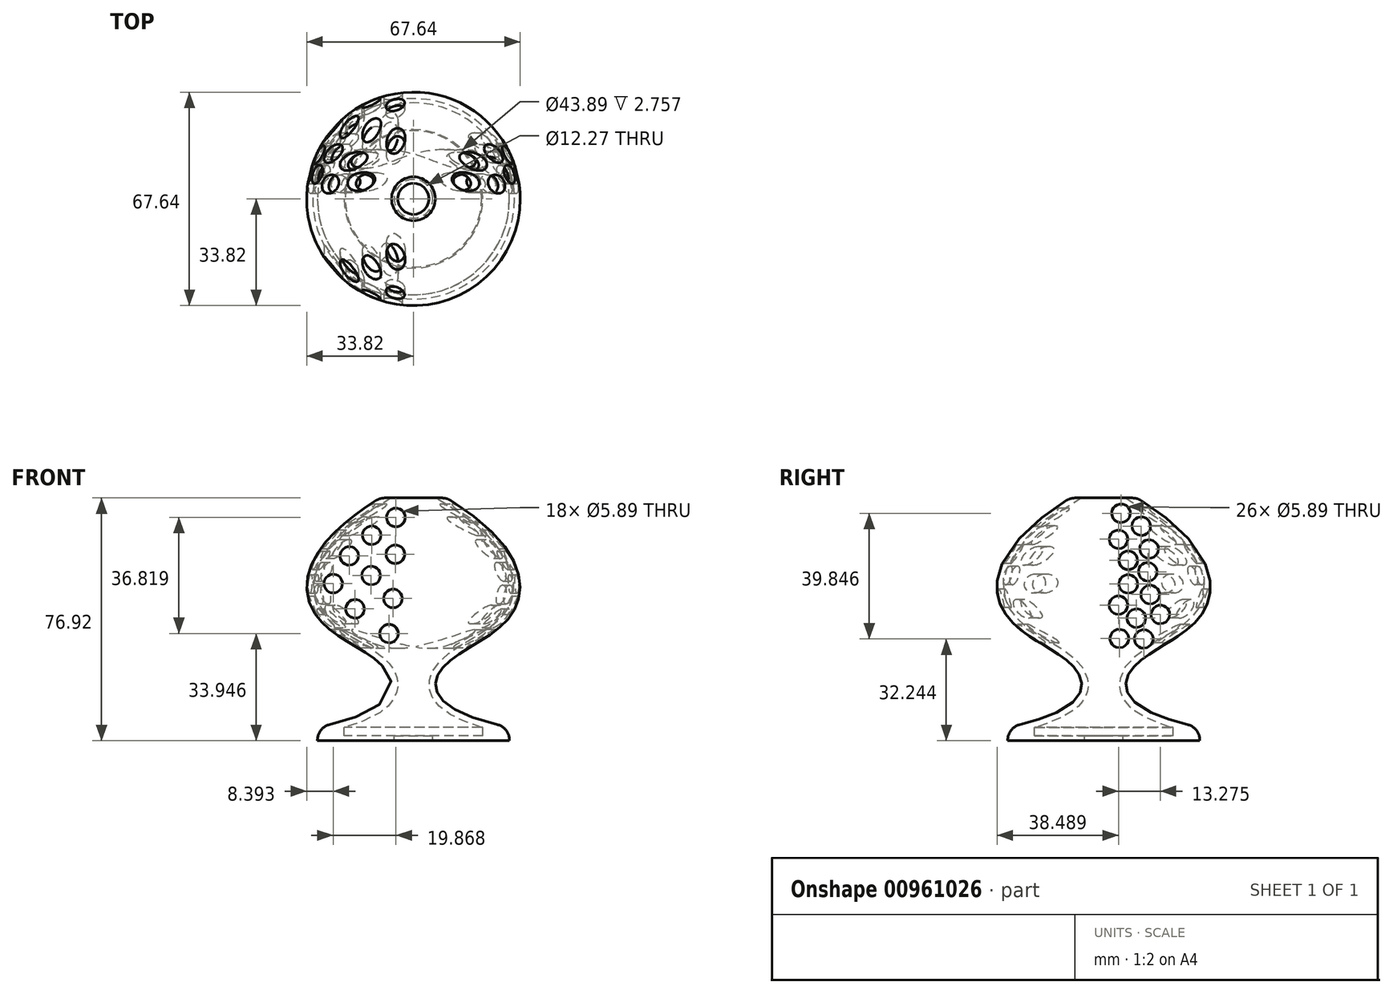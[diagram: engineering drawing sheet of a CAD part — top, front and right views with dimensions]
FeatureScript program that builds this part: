
annotation { "Feature Type Name" : "Feature", "Feature Type Description" : "" }
export const myFeature = defineFeature(function(context is Context, id is Id, definition is map)
    precondition{}
    {
        {
            var Q0;
            Q0=qCreatedBy(makeId("Front.planeOp"),FACE);
            var sketch = newSketch(context, id + "F0", { "sketchPlane" : qUnion([Q0])});
            skLineSegment(sketch, "E0", {"start": v(0, 0) * mm, "end": v(-30.41, 0) * mm});
            skFitSpline(sketch, "E1", {"points": [v(-30.41, 0) * mm, v(-9.34, 18.95) * mm, v(-30.19, 34.63) * mm, v(0, 78.45) * mm], "startDerivative": vector(248.38, 50.2) * mm, "endDerivative": vector(258.38, 128.89) * mm});
            skLineSegment(sketch, "E2", {"start": v(0, 78.45) * mm, "end": v(0, 74.71) * mm});
            skFitSpline(sketch, "E3.0", {"points": [v(-30.02, -1.96) * mm, v(-27.39, -1.43) * mm, v(-22.63, -0.3) * mm, v(-16.88, 1.6) * mm, v(-12.37, 3.66) * mm, v(-8.97, 5.91) * mm, v(-6.97, 7.97) * mm, v(-5.87, 9.74) * mm, v(-5.3, 11.12) * mm, v(-5, 12.53) * mm, v(-4.95, 13.93) * mm, v(-5.14, 15.3) * mm, v(-5.66, 17.02) * mm, v(-6.74, 19) * mm, v(-8.5, 21.08) * mm, v(-10.59, 22.92) * mm, v(-13.68, 25.15) * mm, v(-17.92, 27.7) * mm, v(-22.16, 30.28) * mm, v(-25.2, 32.5) * mm, v(-26.9, 33.99) * mm, v(-28.1, 35.24) * mm, v(-29.18, 36.54) * mm, v(-30.31, 38.27) * mm, v(-31.27, 40.51) * mm, v(-31.8, 42.9) * mm, v(-31.87, 45.48) * mm, v(-31.4, 48.25) * mm, v(-30.33, 51.24) * mm, v(-27.96, 55.49) * mm, v(-23.07, 61.28) * mm, v(-13.54, 68.77) * mm, v(-4.43, 74.01) * mm, v(0.9, 76.66) * mm]});
            skLineSegment(sketch, "E4", {"start": v(0, 70.9) * mm, "end": v(0, -14.77) * mm, "construction": true});
            skCircle(sketch, "E5", {"center": v(-5.56, 66.52) * mm, "radius": 2.94 * mm});
            skCircle(sketch, "E6", {"center": v(-13.21, 60.87) * mm, "radius": 2.94 * mm});
            skCircle(sketch, "E7", {"center": v(-5.74, 54.86) * mm, "radius": 2.94 * mm});
            skCircle(sketch, "E8", {"center": v(-13.4, 48.12) * mm, "radius": 2.94 * mm});
            skCircle(sketch, "E9", {"center": v(-6.47, 40.82) * mm, "radius": 2.94 * mm});
            skCircle(sketch, "E10", {"center": v(-7.75, 29.7) * mm, "radius": 2.94 * mm});
            skCircle(sketch, "E11", {"center": v(-18.5, 37.54) * mm, "radius": 2.94 * mm});
            skCircle(sketch, "E12", {"center": v(-25.43, 45.56) * mm, "radius": 2.94 * mm});
            skCircle(sketch, "E13", {"center": v(-20.32, 54.31) * mm, "radius": 2.94 * mm});
            skCircle(sketch, "E14.MirrorC", {"center": v(5.56, 66.52) * mm, "radius": 2.94 * mm});
            skCircle(sketch, "E15.MirrorC", {"center": v(25.43, 45.56) * mm, "radius": 2.94 * mm});
            skCircle(sketch, "E16.MirrorC", {"center": v(13.4, 48.12) * mm, "radius": 2.94 * mm});
            skCircle(sketch, "E17.MirrorC", {"center": v(7.75, 29.7) * mm, "radius": 2.94 * mm});
            skCircle(sketch, "E18.MirrorC", {"center": v(13.21, 60.87) * mm, "radius": 2.94 * mm});
            skCircle(sketch, "E19.MirrorC", {"center": v(6.47, 40.82) * mm, "radius": 2.94 * mm});
            skCircle(sketch, "E20.MirrorC", {"center": v(18.5, 37.54) * mm, "radius": 2.94 * mm});
            skCircle(sketch, "E21.MirrorC", {"center": v(5.74, 54.86) * mm, "radius": 2.94 * mm});
            skCircle(sketch, "E22.MirrorC", {"center": v(20.32, 54.31) * mm, "radius": 2.94 * mm});
            skLineSegment(sketch, "E23", {"start": v(-30.41, 0) * mm, "end": v(-30.41, -4.24) * mm});
            skLineSegment(sketch, "E24", {"start": v(-30.41, -4.24) * mm, "end": v(0, -4.24) * mm});
            skLineSegment(sketch, "E25", {"start": v(-21.94, 0) * mm, "end": v(-21.94, -2.76) * mm});
            skLineSegment(sketch, "E26", {"start": v(-21.94, -2.76) * mm, "end": v(0, -2.76) * mm});
            skLineSegment(sketch, "E27", {"start": v(0, -2.76) * mm, "end": v(0, -4.24) * mm});
            skSolve(sketch);
        }
        {
            var Q0;
            {var subQ0=sQuery(id+"F0.wireOp",EDGE,"E1");Q0=makeQuery(id+"F0.imprint","IMPRINT",FACE,{"disambiguationData":[TD([[makeQuery(id+"F0.imprint","IMPRINT",EDGE,{"derivedFrom":subQ0}),-1.0]])]});}
            var Q1;
            {var subQ1=sQuery(id+"F0.wireOp",EDGE,"E23");Q1=makeQuery(id+"F0.imprint","IMPRINT",FACE,{"disambiguationData":[TD([[makeQuery(id+"F0.imprint","IMPRINT",EDGE,{"derivedFrom":subQ1}),1.0]])]});}
            var Q2;
            Q2=sQuery(id+"F0.wireOp",EDGE,"E4");
            revolve(context, id + "F1", {"surfaceOperationType" : NewSurfaceOperationType.NEW, "entities" : qUnion([Q0, Q1]), "axis" : qUnion([Q2]), "revolveType" : RevolveType.FULL});
        }
        {
            var Q0;
            Q0=makeQuery(id+"F0.imprint","IMPRINT",FACE,{"disambiguationData":[TD([[makeQuery(id+"F0.imprint","IMPRINT",EDGE,{"derivedFrom":sQuery(id+"F0.wireOp",EDGE,"E5")}),1.0]])]});
            var Q1;
            Q1=makeQuery(id+"F0.imprint","IMPRINT",FACE,{"disambiguationData":[TD([[makeQuery(id+"F0.imprint","IMPRINT",EDGE,{"derivedFrom":sQuery(id+"F0.wireOp",EDGE,"E14.MirrorC")}),-1.0]])]});
            var Q2;
            Q2=makeQuery(id+"F0.imprint","IMPRINT",FACE,{"disambiguationData":[TD([[makeQuery(id+"F0.imprint","IMPRINT",EDGE,{"derivedFrom":sQuery(id+"F0.wireOp",EDGE,"E21.MirrorC")}),-1.0]])]});
            var Q3;
            Q3=makeQuery(id+"F0.imprint","IMPRINT",FACE,{"disambiguationData":[TD([[makeQuery(id+"F0.imprint","IMPRINT",EDGE,{"derivedFrom":sQuery(id+"F0.wireOp",EDGE,"E18.MirrorC")}),-1.0]])]});
            var Q4;
            Q4=makeQuery(id+"F0.imprint","IMPRINT",FACE,{"disambiguationData":[TD([[makeQuery(id+"F0.imprint","IMPRINT",EDGE,{"derivedFrom":sQuery(id+"F0.wireOp",EDGE,"E22.MirrorC")}),-1.0]])]});
            var Q5;
            Q5=makeQuery(id+"F0.imprint","IMPRINT",FACE,{"disambiguationData":[TD([[makeQuery(id+"F0.imprint","IMPRINT",EDGE,{"derivedFrom":sQuery(id+"F0.wireOp",EDGE,"E16.MirrorC")}),-1.0]])]});
            var Q6;
            Q6=makeQuery(id+"F0.imprint","IMPRINT",FACE,{"disambiguationData":[TD([[makeQuery(id+"F0.imprint","IMPRINT",EDGE,{"derivedFrom":sQuery(id+"F0.wireOp",EDGE,"E19.MirrorC")}),-1.0]])]});
            var Q7;
            Q7=makeQuery(id+"F0.imprint","IMPRINT",FACE,{"disambiguationData":[TD([[makeQuery(id+"F0.imprint","IMPRINT",EDGE,{"derivedFrom":sQuery(id+"F0.wireOp",EDGE,"E17.MirrorC")}),-1.0]])]});
            var Q8;
            Q8=makeQuery(id+"F0.imprint","IMPRINT",FACE,{"disambiguationData":[TD([[makeQuery(id+"F0.imprint","IMPRINT",EDGE,{"derivedFrom":sQuery(id+"F0.wireOp",EDGE,"E20.MirrorC")}),-1.0]])]});
            var Q9;
            Q9=makeQuery(id+"F0.imprint","IMPRINT",FACE,{"disambiguationData":[TD([[makeQuery(id+"F0.imprint","IMPRINT",EDGE,{"derivedFrom":sQuery(id+"F0.wireOp",EDGE,"E15.MirrorC")}),-1.0]])]});
            var Q10;
            Q10=makeQuery(id+"F0.imprint","IMPRINT",FACE,{"disambiguationData":[TD([[makeQuery(id+"F0.imprint","IMPRINT",EDGE,{"derivedFrom":sQuery(id+"F0.wireOp",EDGE,"E7")}),1.0]])]});
            var Q11;
            Q11=makeQuery(id+"F0.imprint","IMPRINT",FACE,{"disambiguationData":[TD([[makeQuery(id+"F0.imprint","IMPRINT",EDGE,{"derivedFrom":sQuery(id+"F0.wireOp",EDGE,"E6")}),1.0]])]});
            var Q12;
            Q12=makeQuery(id+"F0.imprint","IMPRINT",FACE,{"disambiguationData":[TD([[makeQuery(id+"F0.imprint","IMPRINT",EDGE,{"derivedFrom":sQuery(id+"F0.wireOp",EDGE,"E13")}),1.0]])]});
            var Q13;
            Q13=makeQuery(id+"F0.imprint","IMPRINT",FACE,{"disambiguationData":[TD([[makeQuery(id+"F0.imprint","IMPRINT",EDGE,{"derivedFrom":sQuery(id+"F0.wireOp",EDGE,"E12")}),1.0]])]});
            var Q14;
            Q14=makeQuery(id+"F0.imprint","IMPRINT",FACE,{"disambiguationData":[TD([[makeQuery(id+"F0.imprint","IMPRINT",EDGE,{"derivedFrom":sQuery(id+"F0.wireOp",EDGE,"E11")}),1.0]])]});
            var Q15;
            Q15=makeQuery(id+"F0.imprint","IMPRINT",FACE,{"disambiguationData":[TD([[makeQuery(id+"F0.imprint","IMPRINT",EDGE,{"derivedFrom":sQuery(id+"F0.wireOp",EDGE,"E8")}),1.0]])]});
            var Q16;
            Q16=makeQuery(id+"F0.imprint","IMPRINT",FACE,{"disambiguationData":[TD([[makeQuery(id+"F0.imprint","IMPRINT",EDGE,{"derivedFrom":sQuery(id+"F0.wireOp",EDGE,"E9")}),1.0]])]});
            var Q17;
            Q17=makeQuery(id+"F0.imprint","IMPRINT",FACE,{"disambiguationData":[TD([[makeQuery(id+"F0.imprint","IMPRINT",EDGE,{"derivedFrom":sQuery(id+"F0.wireOp",EDGE,"E10")}),1.0]])]});
            extrude(context, id + "F2", {"entities" : qUnion([Q0, Q1, Q2, Q3, Q4, Q5, Q6, Q7, Q8, Q9, Q10, Q11, Q12, Q13, Q14, Q15, Q16, Q17]), "operationType" : NewBodyOperationType.REMOVE, "endBound" : BoundingType.SYMMETRIC, "oppositeDirection" : true, "depth" : 250 * mm, "offsetDistance" : 25 * mm});
        }
        {
            var Q0;
            Q0=qCreatedBy(makeId("Right.planeOp"),FACE);
            var sketch = newSketch(context, id + "F3", { "sketchPlane" : qUnion([Q0])});
            skCircle(sketch, "E28", {"center": v(5.45, 67.85) * mm, "radius": 2.94 * mm});
            skCircle(sketch, "E29", {"center": v(11.9, 63.76) * mm, "radius": 2.94 * mm});
            skCircle(sketch, "E30", {"center": v(4.67, 59.6) * mm, "radius": 2.94 * mm});
            skCircle(sketch, "E31", {"center": v(14.34, 56.53) * mm, "radius": 2.94 * mm});
            skCircle(sketch, "E32", {"center": v(7.77, 52.91) * mm, "radius": 2.94 * mm});
            skCircle(sketch, "E33", {"center": v(13.95, 49.3) * mm, "radius": 2.94 * mm});
            skCircle(sketch, "E34", {"center": v(10.34, 34.59) * mm, "radius": 2.94 * mm});
            skCircle(sketch, "E35", {"center": v(14.72, 42.07) * mm, "radius": 2.94 * mm});
            skCircle(sketch, "E36", {"center": v(12.66, 28) * mm, "radius": 2.94 * mm});
            skCircle(sketch, "E37", {"center": v(17.94, 35.75) * mm, "radius": 2.94 * mm});
            skCircle(sketch, "E38", {"center": v(4.92, 28.13) * mm, "radius": 2.94 * mm});
            skCircle(sketch, "E39", {"center": v(7.76, 45.43) * mm, "radius": 2.94 * mm});
            skCircle(sketch, "E40", {"center": v(4.67, 38.71) * mm, "radius": 2.94 * mm});
            skLineSegment(sketch, "E41", {"start": v(0, -6.38) * mm, "end": v(0, 72) * mm, "construction": true});
            skCircle(sketch, "E42.MirrorC", {"center": v(-4.92, 28.13) * mm, "radius": 2.94 * mm});
            skCircle(sketch, "E43.MirrorC", {"center": v(-12.66, 28) * mm, "radius": 2.94 * mm});
            skCircle(sketch, "E44.MirrorC", {"center": v(-17.94, 35.75) * mm, "radius": 2.94 * mm});
            skCircle(sketch, "E45.MirrorC", {"center": v(-10.34, 34.59) * mm, "radius": 2.94 * mm});
            skCircle(sketch, "E46.MirrorC", {"center": v(-4.67, 38.71) * mm, "radius": 2.94 * mm});
            skCircle(sketch, "E47.MirrorC", {"center": v(-14.72, 42.07) * mm, "radius": 2.94 * mm});
            skCircle(sketch, "E48.MirrorC", {"center": v(-7.76, 45.43) * mm, "radius": 2.94 * mm});
            skCircle(sketch, "E49.MirrorC", {"center": v(-13.95, 49.3) * mm, "radius": 2.94 * mm});
            skCircle(sketch, "E50.MirrorC", {"center": v(-14.34, 56.53) * mm, "radius": 2.94 * mm});
            skCircle(sketch, "E51.MirrorC", {"center": v(-7.77, 52.91) * mm, "radius": 2.94 * mm});
            skCircle(sketch, "E52.MirrorC", {"center": v(-4.67, 59.6) * mm, "radius": 2.94 * mm});
            skCircle(sketch, "E53.MirrorC", {"center": v(-11.9, 63.76) * mm, "radius": 2.94 * mm});
            skCircle(sketch, "E54.MirrorC", {"center": v(-5.45, 67.85) * mm, "radius": 2.94 * mm});
            skSolve(sketch);
        }
        {
            var Q0;
            Q0=makeQuery(id+"F3.imprint","IMPRINT",FACE,{"disambiguationData":[TD([[makeQuery(id+"F3.imprint","IMPRINT",EDGE,{"derivedFrom":sQuery(id+"F3.wireOp",EDGE,"E28")}),1.0]])]});
            var Q1;
            Q1=makeQuery(id+"F3.imprint","IMPRINT",FACE,{"disambiguationData":[TD([[makeQuery(id+"F3.imprint","IMPRINT",EDGE,{"derivedFrom":sQuery(id+"F3.wireOp",EDGE,"E29")}),1.0]])]});
            var Q2;
            Q2=makeQuery(id+"F3.imprint","IMPRINT",FACE,{"disambiguationData":[TD([[makeQuery(id+"F3.imprint","IMPRINT",EDGE,{"derivedFrom":sQuery(id+"F3.wireOp",EDGE,"E30")}),1.0]])]});
            var Q3;
            Q3=makeQuery(id+"F3.imprint","IMPRINT",FACE,{"disambiguationData":[TD([[makeQuery(id+"F3.imprint","IMPRINT",EDGE,{"derivedFrom":sQuery(id+"F3.wireOp",EDGE,"E31")}),1.0]])]});
            var Q4;
            Q4=makeQuery(id+"F3.imprint","IMPRINT",FACE,{"disambiguationData":[TD([[makeQuery(id+"F3.imprint","IMPRINT",EDGE,{"derivedFrom":sQuery(id+"F3.wireOp",EDGE,"E32")}),1.0]])]});
            var Q5;
            Q5=makeQuery(id+"F3.imprint","IMPRINT",FACE,{"disambiguationData":[TD([[makeQuery(id+"F3.imprint","IMPRINT",EDGE,{"derivedFrom":sQuery(id+"F3.wireOp",EDGE,"E33")}),1.0]])]});
            var Q6;
            Q6=makeQuery(id+"F3.imprint","IMPRINT",FACE,{"disambiguationData":[TD([[makeQuery(id+"F3.imprint","IMPRINT",EDGE,{"derivedFrom":sQuery(id+"F3.wireOp",EDGE,"E39")}),1.0]])]});
            var Q7;
            Q7=makeQuery(id+"F3.imprint","IMPRINT",FACE,{"disambiguationData":[TD([[makeQuery(id+"F3.imprint","IMPRINT",EDGE,{"derivedFrom":sQuery(id+"F3.wireOp",EDGE,"E35")}),1.0]])]});
            var Q8;
            Q8=makeQuery(id+"F3.imprint","IMPRINT",FACE,{"disambiguationData":[TD([[makeQuery(id+"F3.imprint","IMPRINT",EDGE,{"derivedFrom":sQuery(id+"F3.wireOp",EDGE,"E37")}),1.0]])]});
            var Q9;
            Q9=makeQuery(id+"F3.imprint","IMPRINT",FACE,{"disambiguationData":[TD([[makeQuery(id+"F3.imprint","IMPRINT",EDGE,{"derivedFrom":sQuery(id+"F3.wireOp",EDGE,"E34")}),1.0]])]});
            var Q10;
            Q10=makeQuery(id+"F3.imprint","IMPRINT",FACE,{"disambiguationData":[TD([[makeQuery(id+"F3.imprint","IMPRINT",EDGE,{"derivedFrom":sQuery(id+"F3.wireOp",EDGE,"E36")}),1.0]])]});
            var Q11;
            Q11=makeQuery(id+"F3.imprint","IMPRINT",FACE,{"disambiguationData":[TD([[makeQuery(id+"F3.imprint","IMPRINT",EDGE,{"derivedFrom":sQuery(id+"F3.wireOp",EDGE,"E40")}),1.0]])]});
            var Q12;
            Q12=makeQuery(id+"F3.imprint","IMPRINT",FACE,{"disambiguationData":[TD([[makeQuery(id+"F3.imprint","IMPRINT",EDGE,{"derivedFrom":sQuery(id+"F3.wireOp",EDGE,"E38")}),1.0]])]});
            var Q13;
            Q13=makeQuery(id+"F3.imprint","IMPRINT",FACE,{"disambiguationData":[TD([[makeQuery(id+"F3.imprint","IMPRINT",EDGE,{"derivedFrom":sQuery(id+"F3.wireOp",EDGE,"E54.MirrorC")}),-1.0]])]});
            var Q14;
            Q14=makeQuery(id+"F3.imprint","IMPRINT",FACE,{"disambiguationData":[TD([[makeQuery(id+"F3.imprint","IMPRINT",EDGE,{"derivedFrom":sQuery(id+"F3.wireOp",EDGE,"E53.MirrorC")}),-1.0]])]});
            var Q15;
            Q15=makeQuery(id+"F3.imprint","IMPRINT",FACE,{"disambiguationData":[TD([[makeQuery(id+"F3.imprint","IMPRINT",EDGE,{"derivedFrom":sQuery(id+"F3.wireOp",EDGE,"E52.MirrorC")}),-1.0]])]});
            var Q16;
            Q16=makeQuery(id+"F3.imprint","IMPRINT",FACE,{"disambiguationData":[TD([[makeQuery(id+"F3.imprint","IMPRINT",EDGE,{"derivedFrom":sQuery(id+"F3.wireOp",EDGE,"E50.MirrorC")}),-1.0]])]});
            var Q17;
            Q17=makeQuery(id+"F3.imprint","IMPRINT",FACE,{"disambiguationData":[TD([[makeQuery(id+"F3.imprint","IMPRINT",EDGE,{"derivedFrom":sQuery(id+"F3.wireOp",EDGE,"E51.MirrorC")}),-1.0]])]});
            var Q18;
            Q18=makeQuery(id+"F3.imprint","IMPRINT",FACE,{"disambiguationData":[TD([[makeQuery(id+"F3.imprint","IMPRINT",EDGE,{"derivedFrom":sQuery(id+"F3.wireOp",EDGE,"E49.MirrorC")}),-1.0]])]});
            var Q19;
            Q19=makeQuery(id+"F3.imprint","IMPRINT",FACE,{"disambiguationData":[TD([[makeQuery(id+"F3.imprint","IMPRINT",EDGE,{"derivedFrom":sQuery(id+"F3.wireOp",EDGE,"E48.MirrorC")}),-1.0]])]});
            var Q20;
            Q20=makeQuery(id+"F3.imprint","IMPRINT",FACE,{"disambiguationData":[TD([[makeQuery(id+"F3.imprint","IMPRINT",EDGE,{"derivedFrom":sQuery(id+"F3.wireOp",EDGE,"E47.MirrorC")}),-1.0]])]});
            var Q21;
            Q21=makeQuery(id+"F3.imprint","IMPRINT",FACE,{"disambiguationData":[TD([[makeQuery(id+"F3.imprint","IMPRINT",EDGE,{"derivedFrom":sQuery(id+"F3.wireOp",EDGE,"E45.MirrorC")}),-1.0]])]});
            var Q22;
            Q22=makeQuery(id+"F3.imprint","IMPRINT",FACE,{"disambiguationData":[TD([[makeQuery(id+"F3.imprint","IMPRINT",EDGE,{"derivedFrom":sQuery(id+"F3.wireOp",EDGE,"E46.MirrorC")}),-1.0]])]});
            var Q23;
            Q23=makeQuery(id+"F3.imprint","IMPRINT",FACE,{"disambiguationData":[TD([[makeQuery(id+"F3.imprint","IMPRINT",EDGE,{"derivedFrom":sQuery(id+"F3.wireOp",EDGE,"E44.MirrorC")}),-1.0]])]});
            var Q24;
            Q24=makeQuery(id+"F3.imprint","IMPRINT",FACE,{"disambiguationData":[TD([[makeQuery(id+"F3.imprint","IMPRINT",EDGE,{"derivedFrom":sQuery(id+"F3.wireOp",EDGE,"E43.MirrorC")}),-1.0]])]});
            var Q25;
            Q25=makeQuery(id+"F3.imprint","IMPRINT",FACE,{"disambiguationData":[TD([[makeQuery(id+"F3.imprint","IMPRINT",EDGE,{"derivedFrom":sQuery(id+"F3.wireOp",EDGE,"E42.MirrorC")}),-1.0]])]});
            extrude(context, id + "F4", {"entities" : qUnion([Q0, Q1, Q2, Q3, Q4, Q5, Q6, Q7, Q8, Q9, Q10, Q11, Q12, Q13, Q14, Q15, Q16, Q17, Q18, Q19, Q20, Q21, Q22, Q23, Q24, Q25]), "operationType" : NewBodyOperationType.REMOVE, "endBound" : BoundingType.SYMMETRIC, "oppositeDirection" : true, "depth" : 250 * mm, "offsetDistance" : 25 * mm});
        }
        {
            var Q0;
            Q0=qCreatedBy(makeId("Front.planeOp"),FACE);
            var sketch = newSketch(context, id + "F5", { "sketchPlane" : qUnion([Q0])});
            skLineSegment(sketch, "E55.bottom", {"start": v(-20.8, 85.8) * mm, "end": v(22.4, 85.8) * mm});
            skLineSegment(sketch, "E55.top", {"start": v(-20.8, 72.68) * mm, "end": v(22.4, 72.68) * mm});
            skLineSegment(sketch, "E55.left", {"start": v(-20.8, 85.8) * mm, "end": v(-20.8, 72.68) * mm});
            skLineSegment(sketch, "E55.right", {"start": v(22.4, 85.8) * mm, "end": v(22.4, 72.68) * mm});
            skSolve(sketch);
        }
        {
            var Q0;
            Q0 = qSketchRegion(id + "F5", true);
            extrude(context, id + "F6", {"entities" : qUnion([Q0]), "operationType" : NewBodyOperationType.REMOVE, "endBound" : BoundingType.SYMMETRIC, "oppositeDirection" : true, "depth" : 250 * mm, "offsetDistance" : 25 * mm});
        }
        {
            var Q0;
            Q0=qCreatedBy(makeId("Top.planeOp"),FACE);
            var sketch = newSketch(context, id + "F7", { "sketchPlane" : qUnion([Q0])});
            skCircle(sketch, "E56", {"center": v(0, 0) * mm, "radius": 6.14 * mm});
            skSolve(sketch);
        }
        {
            var Q0;
            Q0=makeQuery(id+"F7.imprint","IMPRINT",FACE,{"disambiguationData":[TD([[makeQuery(id+"F7.imprint","IMPRINT",EDGE,{"derivedFrom":sQuery(id+"F7.wireOp",EDGE,"E56")}),1.0]])]});
            extrude(context, id + "F8", {"entities" : qUnion([Q0]), "operationType" : NewBodyOperationType.REMOVE, "oppositeDirection" : true, "depth" : 250 * mm, "offsetDistance" : 25 * mm});
        }
        {
            var Q0;
            Q0=makeQuery(id+"F6.boolean.opBoolean","INTERSECT",EDGE,{"derivedFrom":[makeQuery(id+"F1.opRevolve","SWEPT_FACE",FACE,{"disambiguationData":[OSD([sQuery(id+"F0.wireOp",EDGE,"E1")])]}),makeQuery(id+"F6.opExtrude","SWEPT_FACE",FACE,{"disambiguationData":[OSD([sQuery(id+"F5.wireOp",EDGE,"E55.top")])]})]});
            var Q1;
            Q1=makeQuery(id+"F1.opRevolve","SWEPT_EDGE",EDGE,{"disambiguationData":[OSD([sQuery(id+"F0.wireOp",EDGE,"E0"),sQuery(id+"F0.wireOp",EDGE,"E1"),sQuery(id+"F0.wireOp",EDGE,"E23")])]});
            fillet(context, id + "F9", {"entities" : qUnion([Q0, Q1]), "radius" : 5 * mm, "tangentPropagation" : true, "allowEdgeOverflow" : false});
        }
    });
